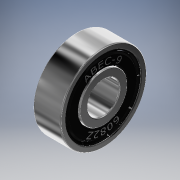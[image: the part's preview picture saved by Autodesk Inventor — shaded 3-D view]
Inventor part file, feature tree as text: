
AUTODESK INVENTOR PART (.ipt)
format: ipt  version: 2019 (Build 230136000, 136)  size: 2,091,520 bytes
history: native  units: mm
features: sketch x13, other x11, revolve x5, pattern_circular x4, extrude x4, mirror x2, projected_geometry x1
ambient origin geometry x8: Origin, YZ Plane, XZ Plane, XY Plane, X Axis, Y Axis, Z Axis, Center Point
bodies: Body1 (feature_tree), Body2 (feature_tree), Body3 (feature_tree), Body4 (feature_tree)
feature tree (40):
  other  "Sólido1"
  revolve  "Revolución1"  [1 undecoded]
  revolve  "Revolución2"  [1 undecoded]
  pattern_circular  "Patrón circular1"  [2 undecoded]
  revolve  "Revolución3"  [1 undecoded]
  extrude  "Extrusión1"  TaperAngle=90.0deg  [1 undecoded]
  pattern_circular  "Patrón circular2"  [2 undecoded]
  mirror  "Simetría1"
  other  "Repujado1"
  other  "Repujado2"
  extrude  "Extrusión2"  Depth=0.3mm
  sketch  "Boceto8"  dims[d30=0.3mm]
  revolve  "Revolución4"  Angle=90.0deg
  pattern_circular  "Patrón circular3"  Count=7 Angle=360.0deg
  sketch  "Boceto10"  dims[d33=0.6mm]
  mirror  "Simetría2"
  extrude  "Extrusión3"  Depth=0.3mm
  extrude  "Extrusión4"  Depth=0.3mm
  revolve  "Revolución5"  [1 undecoded]
  pattern_circular  "Patrón circular4"  [2 undecoded]
  sketch  "Boceto1"  dims[d0=22.0mm d1=8.0mm]
  other  "Imagen2"
  sketch  "Boceto2"  dims[d2=0.3mm d3=7.0mm]
  other  "Sólido2"
  sketch  "Boceto3"  dims[d4=7.0mm]
  other  "Sólido3"
  sketch  "Boceto4"  dims[d5=19.2mm]
  sketch  "Boceto5"  dims[d6=12.15mm]
  sketch  "Boceto6"  dims[d7=0.2mm]
  sketch  "Boceto7"  dims[d23=0.5mm]
  other  "Sólido4"
  projected_geometry  "Contorno proyectado1"
  sketch  "Boceto9"  dims[d31=0.2mm]
  sketch  "Boceto11"  dims[d35=12.217305mm]
  sketch  "Boceto12"  dims[d37=7.0mm]
  sketch  "Boceto13"  dims[d40=4.0mm d42=1.5125mm d43=3.025mm d44=90.0deg d45=3.99mm d46=2.0mm d47=90.0deg d48=70.0mm d49=360.0deg d69=0.3mm d72=0.1mm d76=0.05mm d80=0.15mm d83=0.056mm d84=0.052494mm d85=0.05mm d86=0.2mm d87=0.05mm d90=0.035mm d91=90.0deg d92=0.2mm d93=0.3mm d94=0.3mm d95=10.0mm d96=0.0mm d97=0.18mm d98=0.18mm d99=0.18mm d100=0.18mm d101=90.0mm d102=360.0deg d104=13.5mm d105=0.002mm d106=0.0mm d107=13.5mm d108=13.5mm d109=13.5mm d110=13.5mm d111=0.002mm d112=0.0mm d113=0.75mm d114=0.75mm d115=4.5mm d116=0.0mm d117=0.15mm d120=180.0deg d121=70.0mm d122=360.0deg d124=0.42mm d125=0.0mm d126=0.1mm d127=20.0mm d128=0.0mm d129=0.0mm d130=0.05mm d131=180.0deg d132=70.0mm d133=360.0deg]
  other  "Proyectar aristas de corte1"
  other  "Proyectar aristas de corte2"
  other  "Proyectar aristas de corte3"
  other  "Proyectar aristas de corte4"
note: 11 required parameter values undecoded (feature->parameter linkage not recoverable at this tier; creation-order binding heuristic only, values carry confidence <= 0.55)